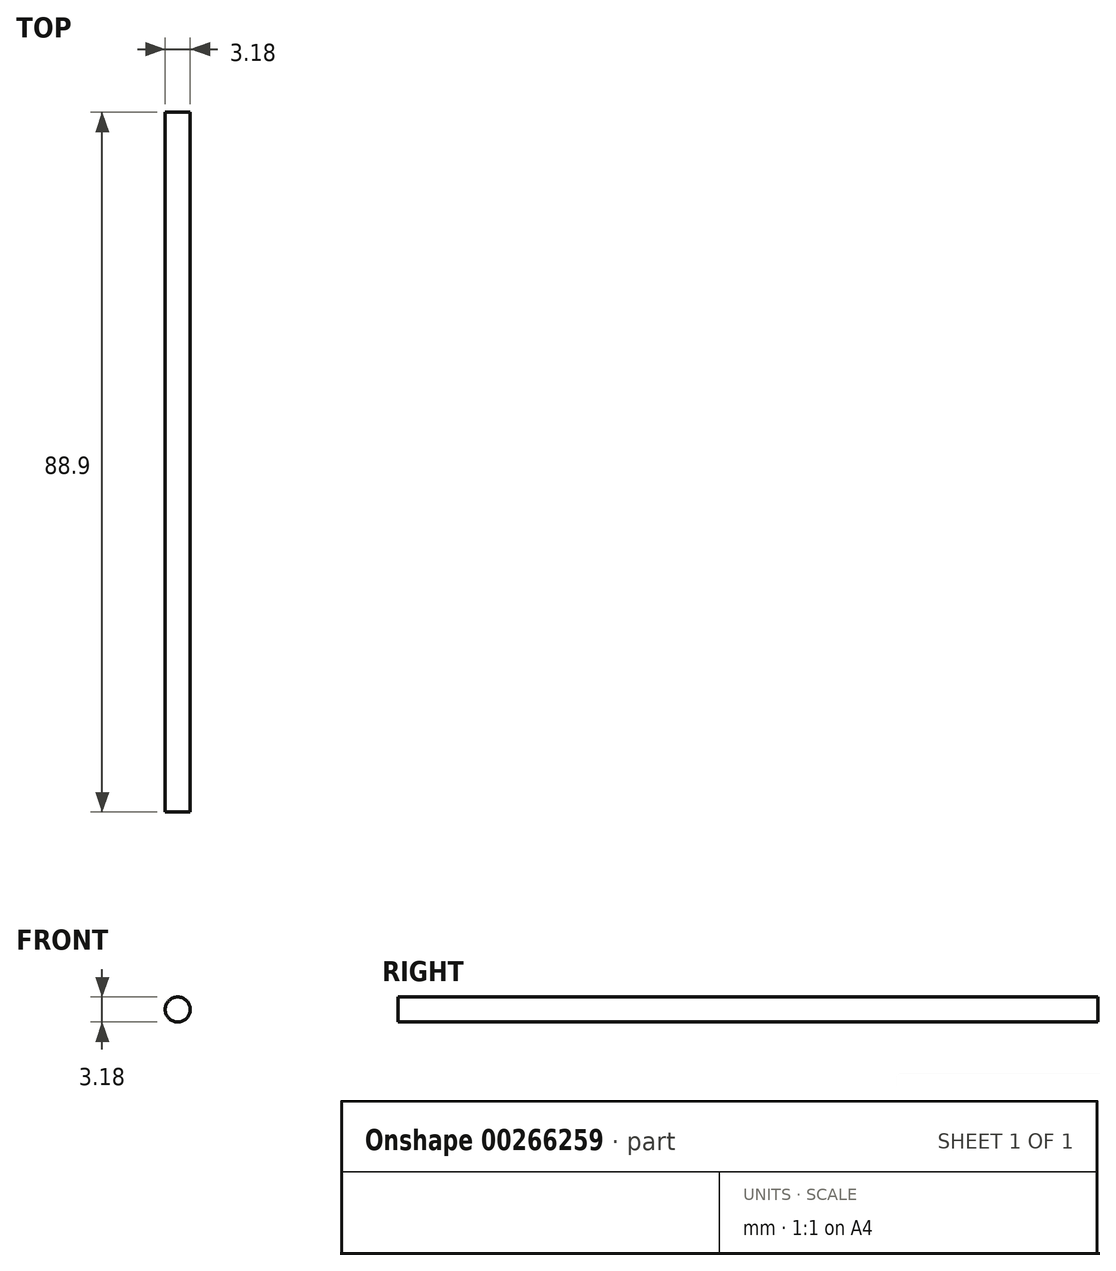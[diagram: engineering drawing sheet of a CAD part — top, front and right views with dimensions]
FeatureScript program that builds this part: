
annotation { "Feature Type Name" : "Feature", "Feature Type Description" : "" }
export const myFeature = defineFeature(function(context is Context, id is Id, definition is map)
    precondition{}
    {
        {
            var Q0;
            Q0=qCreatedBy(makeId("Front.planeOp"),FACE);
            var sketch = newSketch(context, id + "F0", { "sketchPlane" : qUnion([Q0])});
            skCircle(sketch, "E0", {"center": v(0, 0) * mm, "radius": 1.59 * mm});
            skSolve(sketch);
        }
        {
            var Q0;
            Q0=qSketchRegion(id+"F0",true);
            extrude(context, id + "F1", {"entities" : qUnion([Q0]), "depth" : 88.9 * mm});
        }
    });
